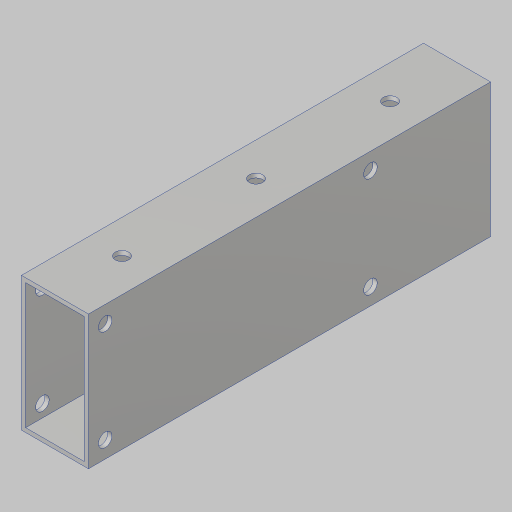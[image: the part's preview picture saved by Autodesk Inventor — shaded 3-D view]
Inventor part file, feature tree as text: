
AUTODESK INVENTOR PART (.ipt)
format: ipt  version: 2023.5 (Build 275446000, 446)  size: 145,920 bytes
history: native  units: in
note: dims shown in document units (in); Inventor stores cm internally (conversion verified against a paired STEP export)
features: hole x3, sketch x3, extrude x1, projected_geometry x1
ambient origin geometry x8: Origin, YZ Plane, XZ Plane, XY Plane, X Axis, Y Axis, Z Axis, Center Point
bodies: Solid1 (feature_tree)
feature tree (8):
  extrude  "Extrusion1"  Depth=4.0in
  hole  "Hole1"  [1 undecoded]
  hole  "Hole3"  [1 undecoded]
  hole  "Hole2"  [1 undecoded]
  sketch  "Sketch2"  dims[d4=0.0in d5=4.0in]
  projected_geometry  "Projected Loop1"
  sketch  "Sketch3"  dims[d6=0.201in d7=0.75in d8=0.385in d9=0.25in d10=0.5635in d11=1.0in d12=0.8108in d14=4.7244in]
  sketch  "Sketch4"  dims[d15=3.7402in d16=4.2323in d17=1.5in d18=0.156in d19=0.38in d20=0.375in d21=0.25in d22=0.5635in d23=1.0in d24=0.8108in d25=4.2323in d27=0.25in d28=1.5in d29=0.201in d30=0.38in d31=0.385in d32=0.25in d33=0.5635in d34=1.0in d35=0.8108in]
note: 3 required parameter values undecoded (feature->parameter linkage not recoverable at this tier; creation-order binding heuristic only, values carry confidence <= 0.55)
